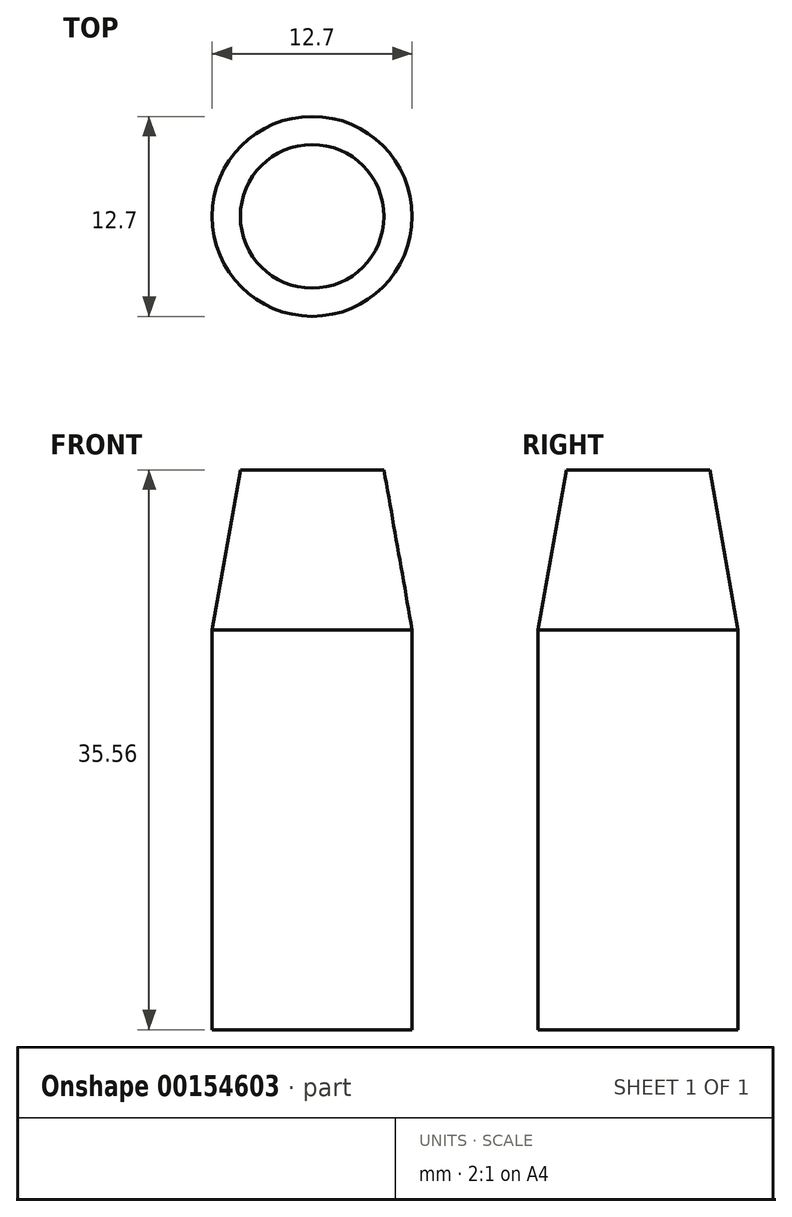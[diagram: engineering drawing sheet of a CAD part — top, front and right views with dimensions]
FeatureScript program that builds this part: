
annotation { "Feature Type Name" : "Feature", "Feature Type Description" : "" }
export const myFeature = defineFeature(function(context is Context, id is Id, definition is map)
    precondition{}
    {
        {
            var Q0;
            Q0=qCreatedBy(makeId("Top.planeOp"),FACE);
            var sketch = newSketch(context, id + "F1", { "sketchPlane" : qUnion([Q0])});
            skCircle(sketch, "E0", {"center": v(0, 0) * mm, "radius": 6.35 * mm});
            skSolve(sketch);
        }
        {
            var Q0;
            Q0=makeQuery(id+"F1.imprint","IMPRINT",FACE,{"disambiguationData":[TD([[makeQuery(id+"F1.imprint","IMPRINT",EDGE,{"derivedFrom":sQuery(id+"F1.wireOp",EDGE,"E0")}),1.0]])]});
            extrude(context, id + "F0", {"entities" : qUnion([Q0]), "depth" : 25.4 * mm, "symmetric" : true});
        }
        {
            var Q0;
            Q0=makeQuery(id+"F0.opExtrude","CAP_FACE",FACE,{"disambiguationData":[OSD([sQuery(id+"F1.wireOp",EDGE,"E0")])],"isStart":false});
            extrude(context, id + "F2", {"entities" : qUnion([Q0]), "operationType" : NewBodyOperationType.ADD, "depth" : 10.16 * mm, "hasDraft" : true, "draftAngle" : 10 * degree, "draftPullDirection" : true});
        }
    });
